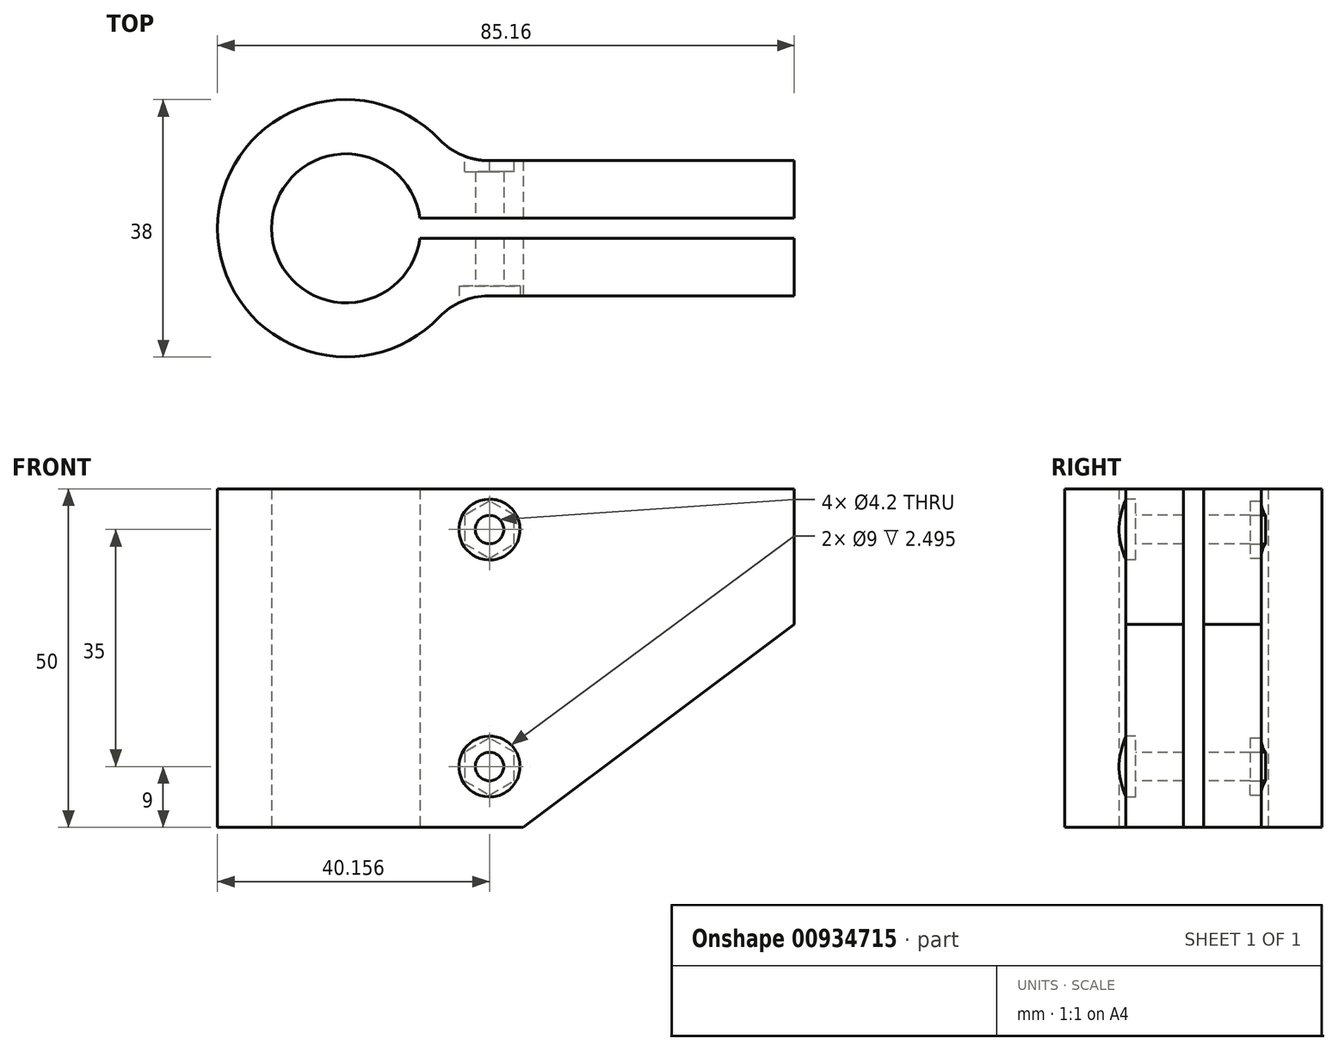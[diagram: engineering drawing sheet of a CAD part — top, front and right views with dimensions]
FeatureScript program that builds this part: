
annotation { "Feature Type Name" : "Feature", "Feature Type Description" : "" }
export const myFeature = defineFeature(function(context is Context, id is Id, definition is map)
    precondition{}
    {
        {
            var Q0;
            Q0=qCreatedBy(makeId("Top.planeOp"),FACE);
            var sketch = newSketch(context, id + "F0", { "sketchPlane" : qUnion([Q0])});
            skCircle(sketch, "E0", {"center": v(0, 0) * mm, "radius": 11 * mm});
            skCircle(sketch, "E1", {"center": v(0, 0) * mm, "radius": 19 * mm});
            skLineSegment(sketch, "E2", {"start": v(0, 0) * mm, "end": v(58.34, 0) * mm, "construction": true});
            skLineSegment(sketch, "E3", {"start": v(16.16, 10) * mm, "end": v(66.16, 10) * mm});
            skLineSegment(sketch, "E4", {"start": v(16.16, -10) * mm, "end": v(66.16, -10) * mm});
            skLineSegment(sketch, "E5", {"start": v(66.16, 10) * mm, "end": v(66.16, -10) * mm});
            skLineSegment(sketch, "E6", {"start": v(10.9, 1.5) * mm, "end": v(66.16, 1.5) * mm});
            skLineSegment(sketch, "E7", {"start": v(10.9, -1.5) * mm, "end": v(66.16, -1.5) * mm});
            skSolve(sketch);
        }
        {
            var Q0;
            {var subQ0=sQuery(id+"F0.wireOp",EDGE,"E3");Q0=makeQuery(id+"F0.imprint","IMPRINT",FACE,{"disambiguationData":[TD([[makeQuery(id+"F0.imprint","IMPRINT",EDGE,{"derivedFrom":subQ0}),-1.0]])]});}
            var Q1;
            {var subQ5=sQuery(id+"F0.wireOp",EDGE,"E6");var subQ7=sQuery(id+"F0.wireOp",EDGE,"E0");var subQ9=makeQuery(id+"F0.imprint","INTERSECT",VERTEX,{"derivedFrom":[subQ7,subQ5]});Q1=makeQuery(id+"F0.imprint","IMPRINT",FACE,{"disambiguationData":[TD([[makeQuery(id+"F0.imprint","IMPRINT",EDGE,{"disambiguationData":[TD([[subQ9,-1.0]])],"derivedFrom":subQ7}),-1.0]])]});}
            var Q2;
            {var subQ0=sQuery(id+"F0.wireOp",EDGE,"E4");Q2=makeQuery(id+"F0.imprint","IMPRINT",FACE,{"disambiguationData":[TD([[makeQuery(id+"F0.imprint","IMPRINT",EDGE,{"derivedFrom":subQ0}),1.0]])]});}
            extrude(context, id + "F1", {"entities" : qUnion([Q0, Q1, Q2]), "depth" : 50 * mm, "offsetDistance" : 25 * mm});
        }
        {
            var Q0;
            {var subQ0=sQuery(id+"F0.wireOp",EDGE,"E5");Q0=makeQuery(id+"F1.opExtrude","CAP_EDGE",EDGE,{"disambiguationData":[OSD([subQ0]),TDD([makeQuery(id+"F0.imprint","IMPRINT",EDGE,{"disambiguationData":[TD([[makeQuery(id+"F0.imprint","INTERSECT",VERTEX,{"derivedFrom":[sQuery(id+"F0.wireOp",EDGE,"E4"),subQ0]}),1.0]])],"derivedFrom":subQ0})])],"isStart":true});}
            var Q1;
            {var subQ0=sQuery(id+"F0.wireOp",EDGE,"E5");Q1=makeQuery(id+"F1.opExtrude","CAP_EDGE",EDGE,{"disambiguationData":[OSD([subQ0]),TDD([makeQuery(id+"F0.imprint","IMPRINT",EDGE,{"disambiguationData":[TD([[makeQuery(id+"F0.imprint","INTERSECT",VERTEX,{"derivedFrom":[sQuery(id+"F0.wireOp",EDGE,"E3"),subQ0]}),-1.0]])],"derivedFrom":subQ0})])],"isStart":true});}
            chamfer(context, id + "F2", {"entities" : qUnion([Q0, Q1]), "chamferType" : ChamferType.TWO_OFFSETS, "width1" : 40 * mm, "oppositeDirection" : false, "width2" : 30 * mm, "tangentPropagation" : true});
        }
        {
            var Q0;
            Q0=makeQuery(id+"F1.opExtrude","SWEPT_FACE",FACE,{"disambiguationData":[OSD([sQuery(id+"F0.wireOp",EDGE,"E4")])]});
            var sketch = newSketch(context, id + "F3", { "sketchPlane" : qUnion([Q0])});
            skCircle(sketch, "E8", {"center": v(21.16, 44) * mm, "radius": 2.1 * mm});
            skCircle(sketch, "E9", {"center": v(21.16, 9) * mm, "radius": 2.1 * mm});
            skLineSegment(sketch, "E10", {"start": v(21.16, 44) * mm, "end": v(21.16, 9) * mm, "construction": true});
            skCircle(sketch, "E11", {"center": v(21.16, 44) * mm, "radius": 4.5 * mm});
            skCircle(sketch, "E12", {"center": v(21.16, 9) * mm, "radius": 4.5 * mm});
            skSolve(sketch);
        }
        {
            var Q0;
            Q0=makeQuery(id+"F3.imprint","IMPRINT",FACE,{"disambiguationData":[TD([[makeQuery(id+"F3.imprint","IMPRINT",EDGE,{"derivedFrom":sQuery(id+"F3.wireOp",EDGE,"E8")}),1.0]])]});
            var Q1;
            Q1=makeQuery(id+"F3.imprint","IMPRINT",FACE,{"disambiguationData":[TD([[makeQuery(id+"F3.imprint","IMPRINT",EDGE,{"derivedFrom":sQuery(id+"F3.wireOp",EDGE,"E9")}),1.0]])]});
            extrude(context, id + "F4", {"entities" : qUnion([Q0, Q1]), "operationType" : NewBodyOperationType.REMOVE, "endBound" : BoundingType.THROUGH_ALL, "oppositeDirection" : true, "depth" : 25 * mm, "offsetDistance" : 25 * mm});
        }
        {
            var Q0;
            Q0=makeQuery(id+"F1.opExtrude","SWEPT_EDGE",EDGE,{"disambiguationData":[OSD([sQuery(id+"F0.wireOp",EDGE,"E1"),sQuery(id+"F0.wireOp",EDGE,"E3")])]});
            var Q1;
            Q1=makeQuery(id+"F1.opExtrude","SWEPT_EDGE",EDGE,{"disambiguationData":[OSD([sQuery(id+"F0.wireOp",EDGE,"E1"),sQuery(id+"F0.wireOp",EDGE,"E4")])]});
            fillet(context, id + "F5", {"entities" : qUnion([Q0, Q1]), "tangentPropagation" : true, "radius" : 10 * mm, "defaultsChanged" : true, "vertexSettings" : [], "allowEdgeOverflow" : false});
        }
        {
            var Q0;
            Q0=makeQuery(id+"F3.imprint","IMPRINT",FACE,{"disambiguationData":[TD([[makeQuery(id+"F3.imprint","IMPRINT",EDGE,{"derivedFrom":sQuery(id+"F3.wireOp",EDGE,"E8")}),-1.0]])]});
            var Q1;
            Q1=makeQuery(id+"F3.imprint","IMPRINT",FACE,{"disambiguationData":[TD([[makeQuery(id+"F3.imprint","IMPRINT",EDGE,{"derivedFrom":sQuery(id+"F3.wireOp",EDGE,"E9")}),-1.0]])]});
            extrude(context, id + "F6", {"entities" : qUnion([Q0, Q1]), "operationType" : NewBodyOperationType.REMOVE, "oppositeDirection" : true, "depth" : 3 * mm, "offsetDistance" : 25 * mm, "symmetric" : true});
        }
        {
            var Q0;
            Q0=makeQuery(id+"F1.opExtrude","SWEPT_FACE",FACE,{"disambiguationData":[OSD([sQuery(id+"F0.wireOp",EDGE,"E3")])]});
            var sketch = newSketch(context, id + "F7", { "sketchPlane" : qUnion([Q0])});
            skCircle(sketch, "E13.cCircle", {"center": v(-21.16, 9) * mm, "radius": 3.65 * mm, "construction": true});
            skLineSegment(sketch, "E13.0", {"start": v(-21.16, 4.79) * mm, "end": v(-24.8, 6.9) * mm});
            skLineSegment(sketch, "E13.1", {"start": v(-24.8, 6.9) * mm, "end": v(-24.8, 11.1) * mm});
            skLineSegment(sketch, "E13.2", {"start": v(-24.8, 11.1) * mm, "end": v(-21.16, 13.21) * mm});
            skLineSegment(sketch, "E13.3", {"start": v(-21.16, 13.21) * mm, "end": v(-17.5, 11.1) * mm});
            skLineSegment(sketch, "E13.4", {"start": v(-17.5, 11.1) * mm, "end": v(-17.5, 6.9) * mm});
            skLineSegment(sketch, "E13.5", {"start": v(-17.5, 6.9) * mm, "end": v(-21.16, 4.79) * mm});
            skPoint(sketch, "E13.0.midPoint", {"position": v(-22.98, 5.84) * mm});
            skCircle(sketch, "E14.cCircle", {"center": v(-21.16, 44) * mm, "radius": 3.65 * mm, "construction": true});
            skLineSegment(sketch, "E14.0", {"start": v(-21.16, 39.79) * mm, "end": v(-24.8, 41.9) * mm});
            skLineSegment(sketch, "E14.1", {"start": v(-24.8, 41.9) * mm, "end": v(-24.8, 46.1) * mm});
            skLineSegment(sketch, "E14.2", {"start": v(-24.8, 46.1) * mm, "end": v(-21.16, 48.21) * mm});
            skLineSegment(sketch, "E14.3", {"start": v(-21.16, 48.21) * mm, "end": v(-17.5, 46.1) * mm});
            skLineSegment(sketch, "E14.4", {"start": v(-17.5, 46.1) * mm, "end": v(-17.5, 41.9) * mm});
            skLineSegment(sketch, "E14.5", {"start": v(-17.5, 41.9) * mm, "end": v(-21.16, 39.79) * mm});
            skPoint(sketch, "E14.0.midPoint", {"position": v(-22.98, 40.84) * mm});
            skSolve(sketch);
        }
        {
            var Q0;
            {var subQ12=sQuery(id+"F7.wireOp",EDGE,"E13.0");Q0=makeQuery(id+"F7.imprint","IMPRINT",FACE,{"disambiguationData":[TD([[makeQuery(id+"F7.imprint","IMPRINT",EDGE,{"derivedFrom":subQ12}),-1.0]])]});}
            var Q1;
            {var subQ4=sQuery(id+"F7.wireOp",EDGE,"E13.4");Q1=makeQuery(id+"F7.imprint","IMPRINT",FACE,{"disambiguationData":[TD([[makeQuery(id+"F7.imprint","IMPRINT",EDGE,{"derivedFrom":subQ4}),-1.0]])]});}
            var Q2;
            {var subQ9=sQuery(id+"F7.wireOp",EDGE,"E14.0");Q2=makeQuery(id+"F7.imprint","IMPRINT",FACE,{"disambiguationData":[TD([[makeQuery(id+"F7.imprint","IMPRINT",EDGE,{"derivedFrom":subQ9}),-1.0]])]});}
            var Q3;
            {var subQ4=sQuery(id+"F7.wireOp",EDGE,"E14.4");Q3=makeQuery(id+"F7.imprint","IMPRINT",FACE,{"disambiguationData":[TD([[makeQuery(id+"F7.imprint","IMPRINT",EDGE,{"derivedFrom":subQ4}),-1.0]])]});}
            var Q4;
            Q4=sQuery(id+"F7.wireOp",EDGE,"E13.0");
            var Q5;
            Q5=sQuery(id+"F7.wireOp",EDGE,"E13.1");
            var Q6;
            Q6=sQuery(id+"F7.wireOp",EDGE,"E13.2");
            var Q7;
            Q7=sQuery(id+"F7.wireOp",EDGE,"E13.3");
            var Q8;
            Q8=sQuery(id+"F7.wireOp",EDGE,"E13.4");
            var Q9;
            Q9=sQuery(id+"F7.wireOp",EDGE,"E13.5");
            extrude(context, id + "F8", {"entities" : qUnion([Q0, Q1, Q2, Q3]), "operationType" : NewBodyOperationType.REMOVE, "surfaceEntities" : qUnion([Q4, Q5, Q6, Q7, Q8, Q9]), "oppositeDirection" : true, "depth" : 3.3 * mm, "offsetDistance" : 25 * mm, "symmetric" : true});
        }
    });
